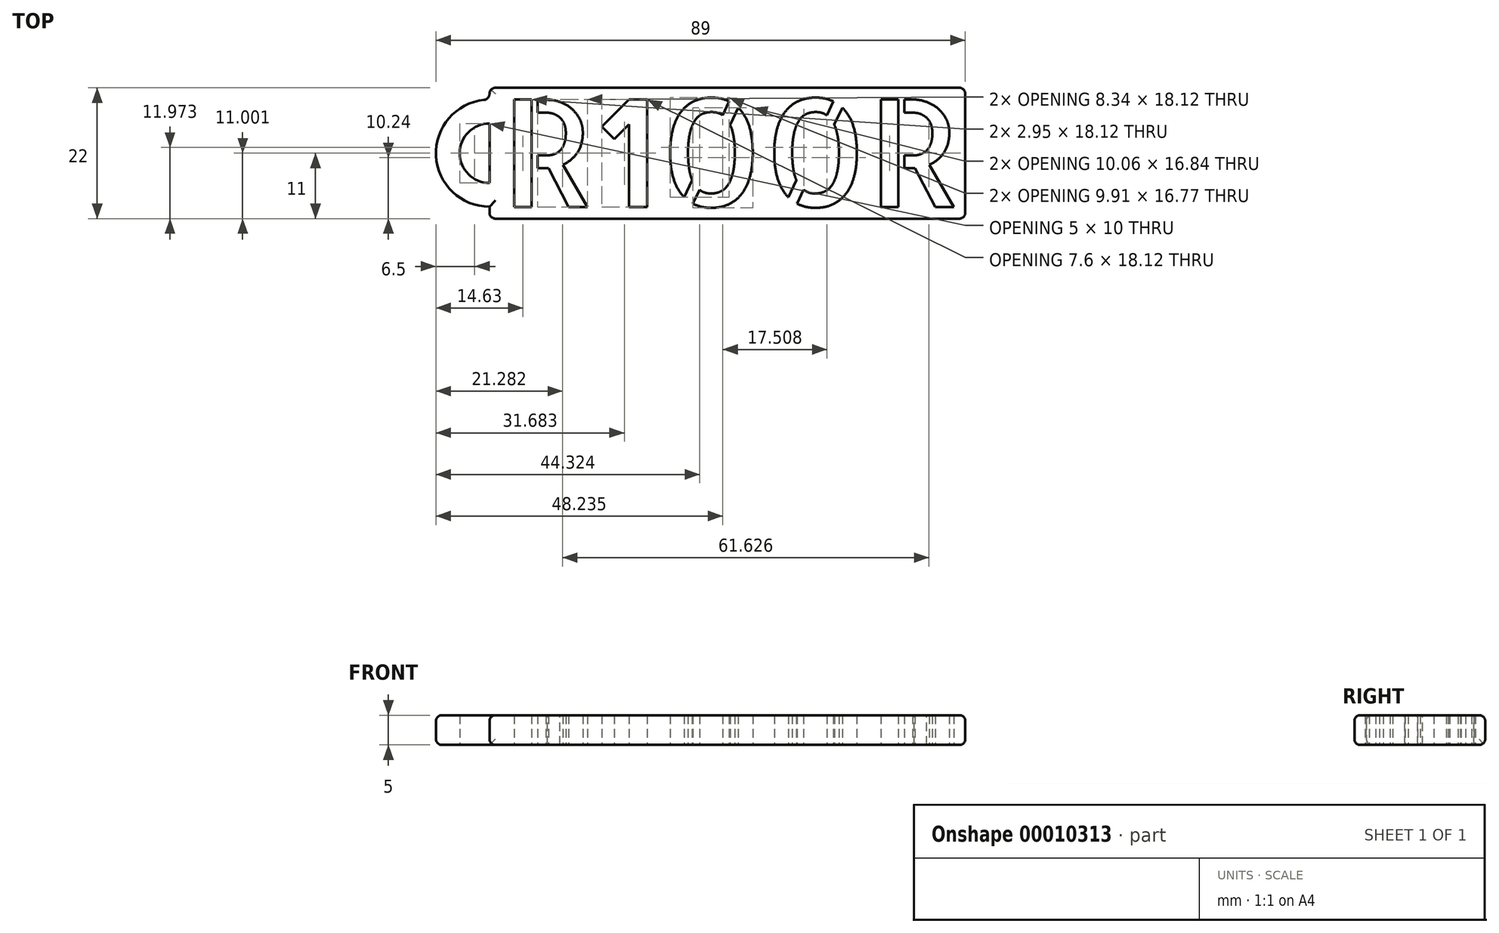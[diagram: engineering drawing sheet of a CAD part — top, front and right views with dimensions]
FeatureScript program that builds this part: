
annotation { "Feature Type Name" : "Feature", "Feature Type Description" : "" }
export const myFeature = defineFeature(function(context is Context, id is Id, definition is map)
    precondition{}
    {
        {
            var Q0;
            Q0=qCreatedBy(makeId("Top.planeOp"),FACE);
            var sketch = newSketch(context, id + "F0", { "sketchPlane" : qUnion([Q0])});
            skText(sketch, "E0", { "text": "R100R", "fontName": "AllertaStencil-Regular.ttf"});
            skLineSegment(sketch, "E1.bottom", {"start": v(-40, 11) * mm, "end": v(40, 11) * mm});
            skLineSegment(sketch, "E1.top", {"start": v(-40, -11) * mm, "end": v(40, -11) * mm});
            skLineSegment(sketch, "E1.left", {"start": v(-40, 11) * mm, "end": v(-40, -11) * mm});
            skLineSegment(sketch, "E1.right", {"start": v(40, 11) * mm, "end": v(40, -11) * mm});
            skLineSegment(sketch, "E2", {"start": v(-38.06, 9.06) * mm, "end": v(-38.06, 11) * mm, "construction": true});
            skLineSegment(sketch, "E3", {"start": v(-38.06, 9.06) * mm, "end": v(-40, 9.06) * mm, "construction": true});
            skArc(sketch, "E4", {"start": v(-40, 5) * mm, "mid": v(-45, 0) * mm, "end": v(-40, -5) * mm});
            skArc(sketch, "E5", {"start": v(-40, 9) * mm, "mid": v(-49, 0) * mm, "end": v(-40, -9) * mm});
            const initialGuessF0  = {"E0": [-0.03806, -0.00906, 1, 0, 0.01813]};
            skSetInitialGuess(sketch, initialGuessF0);
            skSolve(sketch);
        }
        {
            var Q0;
            Q0=makeQuery(id+"F0.imprint","IMPRINT",FACE,{"disambiguationData":[TD([[makeQuery(id+"F0.imprint","IMPRINT",EDGE,{"derivedFrom":sQuery(id+"F0.wireOp",EDGE,"E0.sketch_text.stroke-0")}),1.0]])]});
            var Q1;
            {var subQ1=sQuery(id+"F0.wireOp",EDGE,"E4");Q1=makeQuery(id+"F0.imprint","IMPRINT",FACE,{"disambiguationData":[TD([[makeQuery(id+"F0.imprint","IMPRINT",EDGE,{"derivedFrom":subQ1}),-1.0]])]});}
            extrude(context, id + "F1", {"entities" : qUnion([Q0, Q1]), "depth" : 5 * mm});
        }
        {
            var Q0;
            Q0=makeQuery(id+"F1.opExtrude","CAP_EDGE",EDGE,{"disambiguationData":[OSD([sQuery(id+"F0.wireOp",EDGE,"E1.bottom")])],"isStart":false});
            var Q1;
            {var subQ0=sQuery(id+"F0.wireOp",EDGE,"E1.left");Q1=makeQuery(id+"F1.opExtrude","CAP_EDGE",EDGE,{"disambiguationData":[OSD([subQ0]),TDD([makeQuery(id+"F0.imprint","IMPRINT",EDGE,{"disambiguationData":[TD([[makeQuery(id+"F0.imprint","INTERSECT",VERTEX,{"derivedFrom":[sQuery(id+"F0.wireOp",EDGE,"E1.bottom"),subQ0]}),-1.0]])],"derivedFrom":subQ0})])],"isStart":false});}
            var Q2;
            Q2=makeQuery(id+"F1.opExtrude","CAP_EDGE",EDGE,{"disambiguationData":[OSD([sQuery(id+"F0.wireOp",EDGE,"E5")])],"isStart":false});
            var Q3;
            {var subQ0=sQuery(id+"F0.wireOp",EDGE,"E1.left");var subQ1=sQuery(id+"F0.wireOp",EDGE,"E5");Q3=makeQuery(id+"F1.opExtrude","SWEPT_EDGE",EDGE,{"disambiguationData":[OSD([subQ0,subQ1]),TDD([makeQuery(id+"F0.imprint","INTERSECT",VERTEX,{"disambiguationData":[OD(0.0)],"derivedFrom":[subQ0,subQ1]})])]});}
            var Q4;
            Q4=makeQuery(id+"F1.opExtrude","SWEPT_EDGE",EDGE,{"disambiguationData":[OSD([sQuery(id+"F0.wireOp",EDGE,"E1.bottom"),sQuery(id+"F0.wireOp",EDGE,"E1.left")])]});
            var Q5;
            {var subQ0=sQuery(id+"F0.wireOp",EDGE,"E1.left");Q5=makeQuery(id+"F1.opExtrude","CAP_EDGE",EDGE,{"disambiguationData":[OSD([subQ0]),TDD([makeQuery(id+"F0.imprint","IMPRINT",EDGE,{"disambiguationData":[TD([[makeQuery(id+"F0.imprint","INTERSECT",VERTEX,{"derivedFrom":[sQuery(id+"F0.wireOp",EDGE,"E1.top"),subQ0]}),1.0]])],"derivedFrom":subQ0})])],"isStart":false});}
            var Q6;
            Q6=makeQuery(id+"F1.opExtrude","CAP_EDGE",EDGE,{"disambiguationData":[OSD([sQuery(id+"F0.wireOp",EDGE,"E1.top")])],"isStart":false});
            var Q7;
            Q7=makeQuery(id+"F1.opExtrude","SWEPT_EDGE",EDGE,{"disambiguationData":[OSD([sQuery(id+"F0.wireOp",EDGE,"E1.top"),sQuery(id+"F0.wireOp",EDGE,"E1.left")])]});
            var Q8;
            Q8=makeQuery(id+"F1.opExtrude","CAP_EDGE",EDGE,{"disambiguationData":[OSD([sQuery(id+"F0.wireOp",EDGE,"E1.right")])],"isStart":false});
            var Q9;
            Q9=makeQuery(id+"F1.opExtrude","SWEPT_EDGE",EDGE,{"disambiguationData":[OSD([sQuery(id+"F0.wireOp",EDGE,"E1.bottom"),sQuery(id+"F0.wireOp",EDGE,"E1.right")])]});
            var Q10;
            Q10=makeQuery(id+"F1.opExtrude","CAP_EDGE",EDGE,{"disambiguationData":[OSD([sQuery(id+"F0.wireOp",EDGE,"E1.right")])],"isStart":true});
            var Q11;
            Q11=makeQuery(id+"F1.opExtrude","SWEPT_EDGE",EDGE,{"disambiguationData":[OSD([sQuery(id+"F0.wireOp",EDGE,"E1.top"),sQuery(id+"F0.wireOp",EDGE,"E1.right")])]});
            var Q12;
            Q12=makeQuery(id+"F1.opExtrude","CAP_EDGE",EDGE,{"disambiguationData":[OSD([sQuery(id+"F0.wireOp",EDGE,"E1.top")])],"isStart":true});
            var Q13;
            Q13=makeQuery(id+"F1.opExtrude","CAP_EDGE",EDGE,{"disambiguationData":[OSD([sQuery(id+"F0.wireOp",EDGE,"E1.bottom")])],"isStart":true});
            var Q14;
            Q14=makeQuery(id+"F1.opExtrude","CAP_EDGE",EDGE,{"disambiguationData":[OSD([sQuery(id+"F0.wireOp",EDGE,"E5")])],"isStart":true});
            var Q15;
            {var subQ0=sQuery(id+"F0.wireOp",EDGE,"E1.left");Q15=makeQuery(id+"F1.opExtrude","CAP_EDGE",EDGE,{"disambiguationData":[OSD([subQ0]),TDD([makeQuery(id+"F0.imprint","IMPRINT",EDGE,{"disambiguationData":[TD([[makeQuery(id+"F0.imprint","INTERSECT",VERTEX,{"derivedFrom":[sQuery(id+"F0.wireOp",EDGE,"E1.top"),subQ0]}),1.0]])],"derivedFrom":subQ0})])],"isStart":true});}
            fillet(context, id + "F2", {"entities" : qUnion([Q0, Q1, Q2, Q3, Q4, Q5, Q6, Q7, Q8, Q9, Q10, Q11, Q12, Q13, Q14, Q15]), "radius" : 1 * mm, "tangentPropagation" : true, "allowEdgeOverflow" : false});
        }
    });
